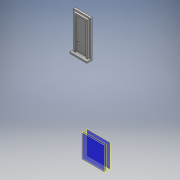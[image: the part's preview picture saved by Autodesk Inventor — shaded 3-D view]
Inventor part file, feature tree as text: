
AUTODESK INVENTOR PART (.ipt)
format: ipt  version: 2016 SP1 (Build 200210100, 210)  size: 136,192 bytes
history: native  units: mm
features: other x7, extrude x4, sketch x4
ambient origin geometry x8: Origin, YZ Plane, XZ Plane, XY Plane, X Axis, Y Axis, Z Axis, Center Point
bodies: Body1 (feature_tree)
feature tree (15):
  other  "Bryła1"
  other  "Płaszczyzna konstrukcyjna1"
  other  "Płaszczyzna konstrukcyjna3"
  other  "Płaszczyzna konstrukcyjna2"
  extrude  "Wyciągnięcie proste21"  Depth=1.5mm
  other  "Płaszczyzna konstrukcyjna5"
  extrude  "Wyciągnięcie proste22"  Depth=1.5mm
  other  "Płaszczyzna konstrukcyjna6"
  extrude  "Wyciągnięcie proste23"  Depth=1.5mm
  other  "Płaszczyzna konstrukcyjna4"
  extrude  "Wyciągnięcie proste25"  Depth=1.5mm TaperAngle=0.0deg
  sketch  "Szkic23"
  sketch  "Szkic24"
  sketch  "Szkic25"
  sketch  "Szkic27"
